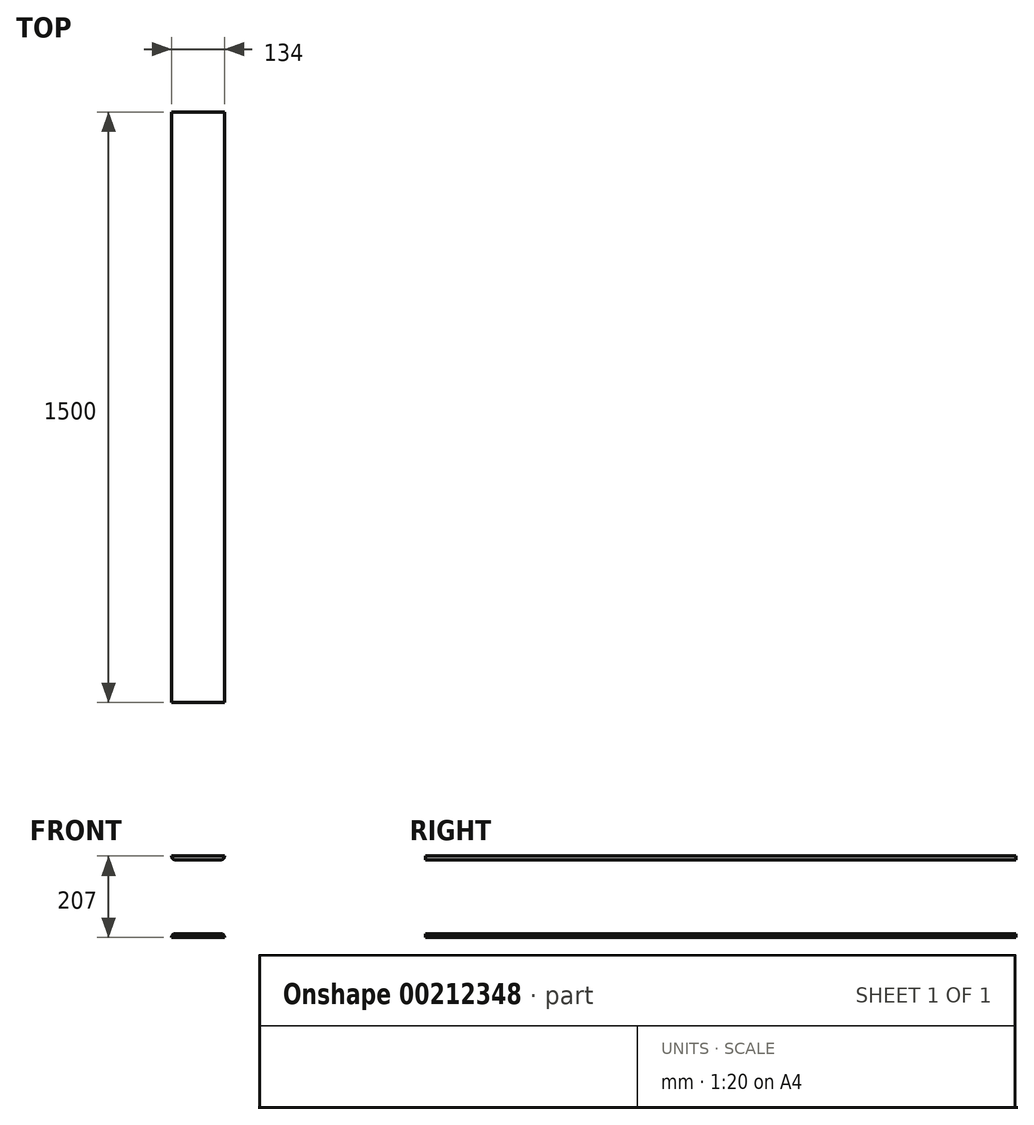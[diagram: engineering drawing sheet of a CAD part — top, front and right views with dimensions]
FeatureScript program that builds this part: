
annotation { "Feature Type Name" : "Feature", "Feature Type Description" : "" }
export const myFeature = defineFeature(function(context is Context, id is Id, definition is map)
    precondition{}
    {
        {
            assignVariable(context, id + "F0", {"name" : "BeamLength", "anyValue" : 1500});
        }
        {
            var Q0;
            Q0=qCreatedBy(makeId("Front.planeOp"),FACE);
            var sketch = newSketch(context, id + "F1", { "sketchPlane" : qUnion([Q0])});
            skLineSegment(sketch, "E0.bottom", {"start": v(-67, 0) * mm, "end": v(67, 0) * mm});
            skLineSegment(sketch, "E0.top", {"start": v(-67, -9.6) * mm, "end": v(67, -9.6) * mm});
            skLineSegment(sketch, "E0.left", {"start": v(-67, 0) * mm, "end": v(-67, -9.6) * mm});
            skLineSegment(sketch, "E0.right", {"start": v(67, 0) * mm, "end": v(67, -9.6) * mm});
            skPoint(sketch, "E1", {"position": v(0, 0) * mm});
            skLineSegment(sketch, "E2.bottom", {"start": v(-67, -197.4) * mm, "end": v(67, -197.4) * mm});
            skLineSegment(sketch, "E2.top", {"start": v(-67, -207) * mm, "end": v(67, -207) * mm});
            skLineSegment(sketch, "E2.left", {"start": v(-67, -197.4) * mm, "end": v(-67, -207) * mm});
            skLineSegment(sketch, "E2.right", {"start": v(67, -197.4) * mm, "end": v(67, -207) * mm});
            skLineSegment(sketch, "E3.bottom", {"start": v(-3.15, -9.6) * mm, "end": v(3.15, -9.6) * mm});
            skLineSegment(sketch, "E3.top", {"start": v(-3.15, -197.4) * mm, "end": v(3.15, -197.4) * mm});
            skLineSegment(sketch, "E3.left", {"start": v(-3.15, -9.6) * mm, "end": v(-3.15, -197.4) * mm});
            skLineSegment(sketch, "E3.right", {"start": v(3.15, -9.6) * mm, "end": v(3.15, -197.4) * mm});
            skPoint(sketch, "E4", {"position": v(0, -9.6) * mm});
            skSolve(sketch);
        }
        {
            var Q0;
            Q0=makeQuery(id+"F1.imprint","IMPRINT",FACE,{"disambiguationData":[TD([[makeQuery(id+"F1.imprint","IMPRINT",EDGE,{"derivedFrom":sQuery(id+"F1.wireOp",EDGE,"E0.bottom")}),-1.0]])]});
            var Q1;
            Q1=makeQuery(id+"F1.imprint","IMPRINT",FACE,{"disambiguationData":[TD([[makeQuery(id+"F1.imprint","IMPRINT",EDGE,{"derivedFrom":sQuery(id+"F1.wireOp",EDGE,"E3.bottom")}),-1.0]])]});
            var Q2;
            Q2=makeQuery(id+"F1.imprint","IMPRINT",FACE,{"disambiguationData":[TD([[makeQuery(id+"F1.imprint","IMPRINT",EDGE,{"derivedFrom":sQuery(id+"F1.wireOp",EDGE,"E2.top")}),1.0]])]});
            extrude(context, id + "F2", {"entities" : qUnion([Q0, Q1, Q2]), "depth" : (getVariable(context, 'BeamLength')) * mm});
        }
        {
            var Q0;
            Q0=makeQuery(id+"F2.opExtrude","SWEPT_EDGE",EDGE,{"disambiguationData":[OSD([sQuery(id+"F1.wireOp",EDGE,"E0.top"),sQuery(id+"F1.wireOp",EDGE,"E3.bottom"),sQuery(id+"F1.wireOp",EDGE,"E3.right")])]});
            var Q1;
            Q1=makeQuery(id+"F2.opExtrude","SWEPT_EDGE",EDGE,{"disambiguationData":[OSD([sQuery(id+"F1.wireOp",EDGE,"E0.top"),sQuery(id+"F1.wireOp",EDGE,"E3.bottom"),sQuery(id+"F1.wireOp",EDGE,"E3.left")])]});
            var Q2;
            Q2=makeQuery(id+"F2.opExtrude","SWEPT_EDGE",EDGE,{"disambiguationData":[OSD([sQuery(id+"F1.wireOp",EDGE,"E2.bottom"),sQuery(id+"F1.wireOp",EDGE,"E3.top"),sQuery(id+"F1.wireOp",EDGE,"E3.right")])]});
            var Q3;
            Q3=makeQuery(id+"F2.opExtrude","SWEPT_EDGE",EDGE,{"disambiguationData":[OSD([sQuery(id+"F1.wireOp",EDGE,"E2.bottom"),sQuery(id+"F1.wireOp",EDGE,"E3.top"),sQuery(id+"F1.wireOp",EDGE,"E3.left")])]});
            fillet(context, id + "F3", {"entities" : qUnion([Q0, Q1, Q2, Q3]), "radius" : 8.9 * mm, "tangentPropagation" : true, "allowEdgeOverflow" : false});
        }
    });
